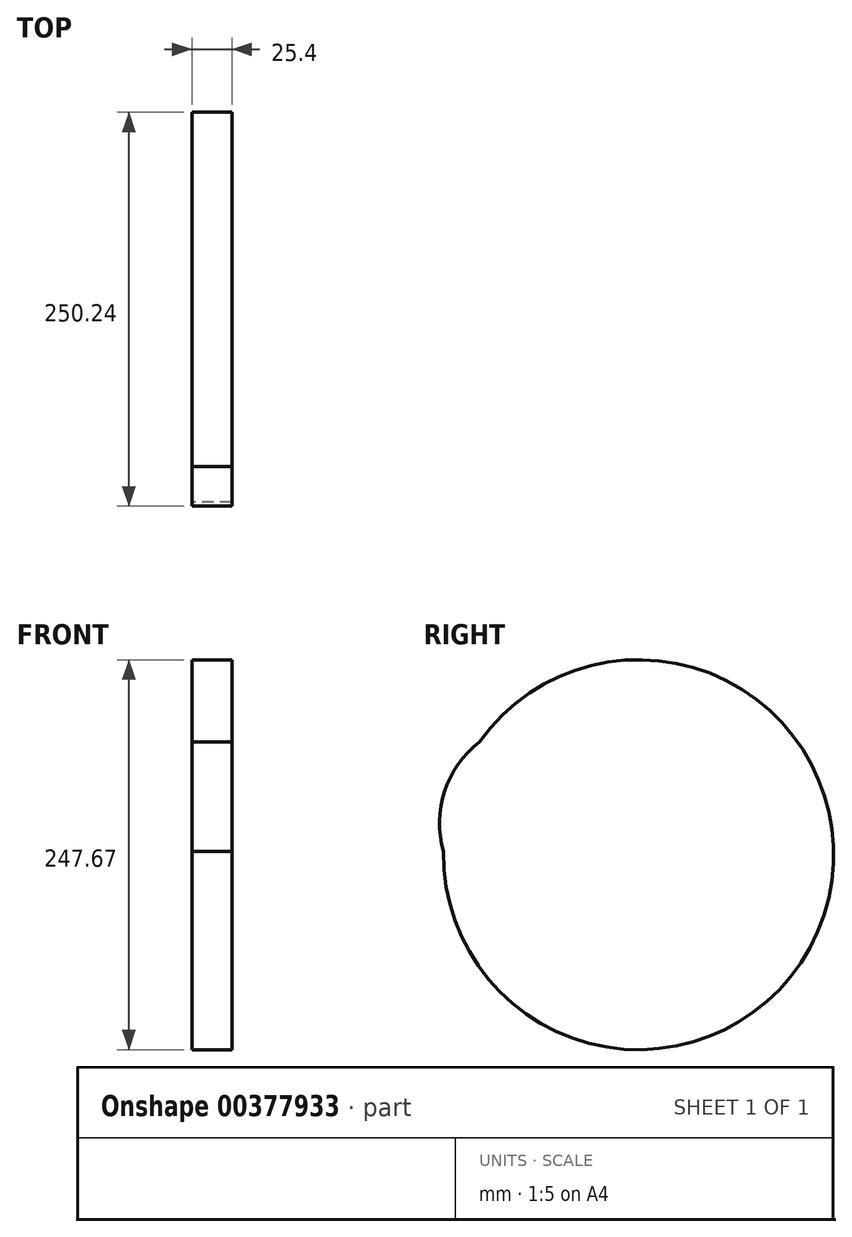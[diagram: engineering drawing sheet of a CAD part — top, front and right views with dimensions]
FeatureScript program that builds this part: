
annotation { "Feature Type Name" : "Feature", "Feature Type Description" : "" }
export const myFeature = defineFeature(function(context is Context, id is Id, definition is map)
    precondition{}
    {
        {
            var Q0;
            Q0=qCreatedBy(makeId("Right.planeOp"),FACE);
            var sketch = newSketch(context, id + "F0", { "sketchPlane" : qUnion([Q0])});
            skCircle(sketch, "E0", {"center": v(0, 0) * mm, "radius": 64.8 * mm});
            skCircle(sketch, "E1", {"center": v(61.6, -20.15) * mm, "radius": 123.83 * mm});
            skLineSegment(sketch, "E2", {"start": v(0, 174.56) * mm, "end": v(-52.1, 140.72) * mm});
            skLineSegment(sketch, "E3", {"start": v(-52.1, 140.72) * mm, "end": v(-52.1, 94.53) * mm});
            skLineSegment(sketch, "E4", {"start": v(-52.1, 94.53) * mm, "end": v(-90.36, -90.21) * mm});
            skSolve(sketch);
        }
        {
            var Q0;
            Q0 = qSketchRegion(id + "F0", true);
            extrude(context, id + "F1", {"entities" : qUnion([Q0]), "endBound" : BoundingType.SYMMETRIC, "depth" : 25.4 * mm});
        }
    });
